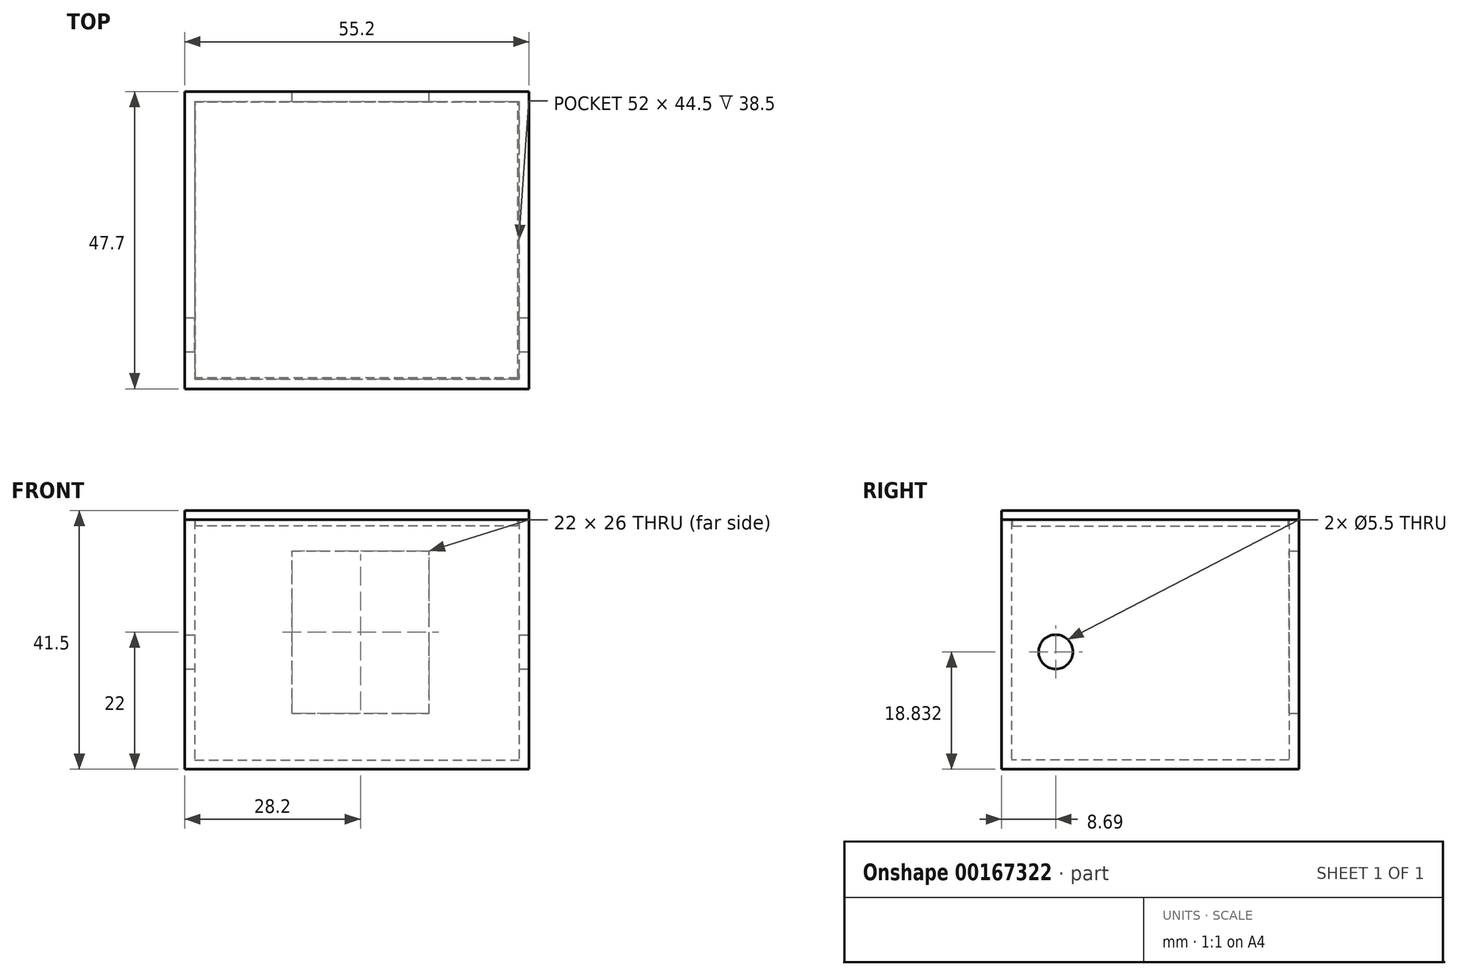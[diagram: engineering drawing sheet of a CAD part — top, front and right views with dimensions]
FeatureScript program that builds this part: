
annotation { "Feature Type Name" : "Feature", "Feature Type Description" : "" }
export const myFeature = defineFeature(function(context is Context, id is Id, definition is map)
    precondition{}
    {
        {
            var Q0;
            Q0=qCreatedBy(makeId("Top.planeOp"),FACE);
            var sketch = newSketch(context, id + "F0", { "sketchPlane" : qUnion([Q0])});
            skLineSegment(sketch, "E0.bottom", {"start": v(26, -22.25) * mm, "end": v(-26, -22.25) * mm});
            skLineSegment(sketch, "E0.top", {"start": v(26, 22.25) * mm, "end": v(-26, 22.25) * mm});
            skLineSegment(sketch, "E0.left", {"start": v(26, -22.25) * mm, "end": v(26, 22.25) * mm});
            skLineSegment(sketch, "E0.right", {"start": v(-26, -22.25) * mm, "end": v(-26, 22.25) * mm});
            skPoint(sketch, "E0.middle", {"position": v(0, 0) * mm});
            skLineSegment(sketch, "E1.bottom", {"start": v(27.6, -23.85) * mm, "end": v(-27.6, -23.85) * mm});
            skLineSegment(sketch, "E1.top", {"start": v(27.6, 23.85) * mm, "end": v(-27.6, 23.85) * mm});
            skLineSegment(sketch, "E1.left", {"start": v(27.6, -23.85) * mm, "end": v(27.6, 23.85) * mm});
            skLineSegment(sketch, "E1.right", {"start": v(-27.6, -23.85) * mm, "end": v(-27.6, 23.85) * mm});
            skSolve(sketch);
        }
        {
            var Q0;
            Q0=makeQuery(id+"F0.imprint","IMPRINT",FACE,{"disambiguationData":[TD([[makeQuery(id+"F0.imprint","IMPRINT",EDGE,{"derivedFrom":sQuery(id+"F0.wireOp",EDGE,"E0.bottom")}),1.0]])]});
            var Q1;
            Q1=makeQuery(id+"F0.imprint","IMPRINT",FACE,{"disambiguationData":[TD([[makeQuery(id+"F0.imprint","IMPRINT",EDGE,{"derivedFrom":sQuery(id+"F0.wireOp",EDGE,"E0.bottom")}),-1.0]])]});
            extrude(context, id + "F1", {"entities" : qUnion([Q0, Q1]), "depth" : 1.5 * mm});
        }
        {
            var Q0;
            Q0 = qSketchRegion(id + "F0", true);
            extrude(context, id + "F2", {"entities" : qUnion([Q0]), "operationType" : NewBodyOperationType.ADD, "depth" : 40 * mm});
        }
        {
            var Q0;
            {var subQ0=sQuery(id+"F0.wireOp",EDGE,"E1.top");Q0=makeQuery(id+"F2.boolean.opBoolean","MERGE",FACE,{"derivedFrom":[makeQuery(id+"F1.opExtrude","SWEPT_FACE",FACE,{"disambiguationData":[OSD([subQ0])]}),makeQuery(id+"F2.opExtrude","SWEPT_FACE",FACE,{"disambiguationData":[OSD([subQ0])]})]});}
            var sketch = newSketch(context, id + "F3", { "sketchPlane" : qUnion([Q0])});
            skLineSegment(sketch, "E2.bottom", {"start": v(10.4, 9) * mm, "end": v(-11.6, 9) * mm});
            skLineSegment(sketch, "E2.top", {"start": v(10.4, 35) * mm, "end": v(-11.6, 35) * mm});
            skLineSegment(sketch, "E2.left", {"start": v(10.4, 9) * mm, "end": v(10.4, 35) * mm});
            skLineSegment(sketch, "E2.right", {"start": v(-11.6, 9) * mm, "end": v(-11.6, 35) * mm});
            skPoint(sketch, "E2.middle", {"position": v(0, 16.45) * mm});
            skSolve(sketch);
        }
        {
            var Q0;
            Q0 = qSketchRegion(id + "F3", true);
            var Q1;
            Q1=makeQuery(id+"F2.opExtrude","SWEPT_FACE",FACE,{"disambiguationData":[OSD([sQuery(id+"F0.wireOp",EDGE,"E0.top")])]});
            extrude(context, id + "F4", {"entities" : qUnion([Q0]), "operationType" : NewBodyOperationType.REMOVE, "endBound" : BoundingType.UP_TO_SURFACE, "oppositeDirection" : true, "endBoundEntityFace" : qUnion([Q1]), "depth" : 25 * mm});
        }
        {
            var Q0;
            {var subQ0=sQuery(id+"F0.wireOp",EDGE,"E1.left");Q0=makeQuery(id+"F2.boolean.opBoolean","MERGE",FACE,{"derivedFrom":[makeQuery(id+"F1.opExtrude","SWEPT_FACE",FACE,{"disambiguationData":[OSD([subQ0])]}),makeQuery(id+"F2.opExtrude","SWEPT_FACE",FACE,{"disambiguationData":[OSD([subQ0])]})]});}
            var sketch = newSketch(context, id + "F5", { "sketchPlane" : qUnion([Q0])});
            skCircle(sketch, "E3", {"center": v(-15.16, 18.83) * mm, "radius": 2.75 * mm});
            skSolve(sketch);
        }
        {
            var Q0;
            Q0 = qSketchRegion(id + "F5", true);
            extrude(context, id + "F6", {"entities" : qUnion([Q0]), "operationType" : NewBodyOperationType.REMOVE, "endBound" : BoundingType.THROUGH_ALL, "oppositeDirection" : true, "depth" : 25 * mm});
        }
        {
            var Q0;
            Q0=makeQuery(id+"F2.opExtrude","CAP_FACE",FACE,{"disambiguationData":[OSD([sQuery(id+"F0.wireOp",EDGE,"E0.bottom"),sQuery(id+"F0.wireOp",EDGE,"E0.top"),sQuery(id+"F0.wireOp",EDGE,"E0.left"),sQuery(id+"F0.wireOp",EDGE,"E0.right"),sQuery(id+"F0.wireOp",EDGE,"E1.bottom"),sQuery(id+"F0.wireOp",EDGE,"E1.top"),sQuery(id+"F0.wireOp",EDGE,"E1.left"),sQuery(id+"F0.wireOp",EDGE,"E1.right")])],"isStart":false});
            var sketch = newSketch(context, id + "F7", { "sketchPlane" : qUnion([Q0])});
            skLineSegment(sketch, "E4.0", {"start": v(-27.6, -23.85) * mm, "end": v(-27.6, 23.85) * mm});
            skLineSegment(sketch, "E4.1", {"start": v(27.6, -23.85) * mm, "end": v(-27.6, -23.85) * mm});
            skLineSegment(sketch, "E4.2", {"start": v(27.6, -23.85) * mm, "end": v(27.6, 23.85) * mm});
            skLineSegment(sketch, "E4.3", {"start": v(27.6, 23.85) * mm, "end": v(-27.6, 23.85) * mm});
            skSolve(sketch);
        }
        {
            var Q0;
            Q0 = qSketchRegion(id + "F7", true);
            extrude(context, id + "F8", {"entities" : qUnion([Q0]), "depth" : 1.5 * mm});
        }
        {
            var Q0;
            Q0=makeQuery(id+"F8.opExtrude","CAP_FACE",FACE,{"disambiguationData":[OSD([sQuery(id+"F7.wireOp",EDGE,"E4.0"),sQuery(id+"F7.wireOp",EDGE,"E4.1"),sQuery(id+"F7.wireOp",EDGE,"E4.2"),sQuery(id+"F7.wireOp",EDGE,"E4.3")])],"isStart":true});
            var sketch = newSketch(context, id + "F9", { "sketchPlane" : qUnion([Q0])});
            skLineSegment(sketch, "E5.0", {"start": v(25.85, -22.1) * mm, "end": v(-25.85, -22.1) * mm});
            skLineSegment(sketch, "E5.1", {"start": v(25.85, 22.1) * mm, "end": v(25.85, -22.1) * mm});
            skLineSegment(sketch, "E5.2", {"start": v(25.85, 22.1) * mm, "end": v(-25.85, 22.1) * mm});
            skLineSegment(sketch, "E5.3", {"start": v(-25.85, 22.1) * mm, "end": v(-25.85, -22.1) * mm});
            skSolve(sketch);
        }
        {
            var Q0;
            Q0 = qSketchRegion(id + "F9", true);
            extrude(context, id + "F10", {"entities" : qUnion([Q0]), "operationType" : NewBodyOperationType.ADD, "depth" : 1 * mm});
        }
    });
